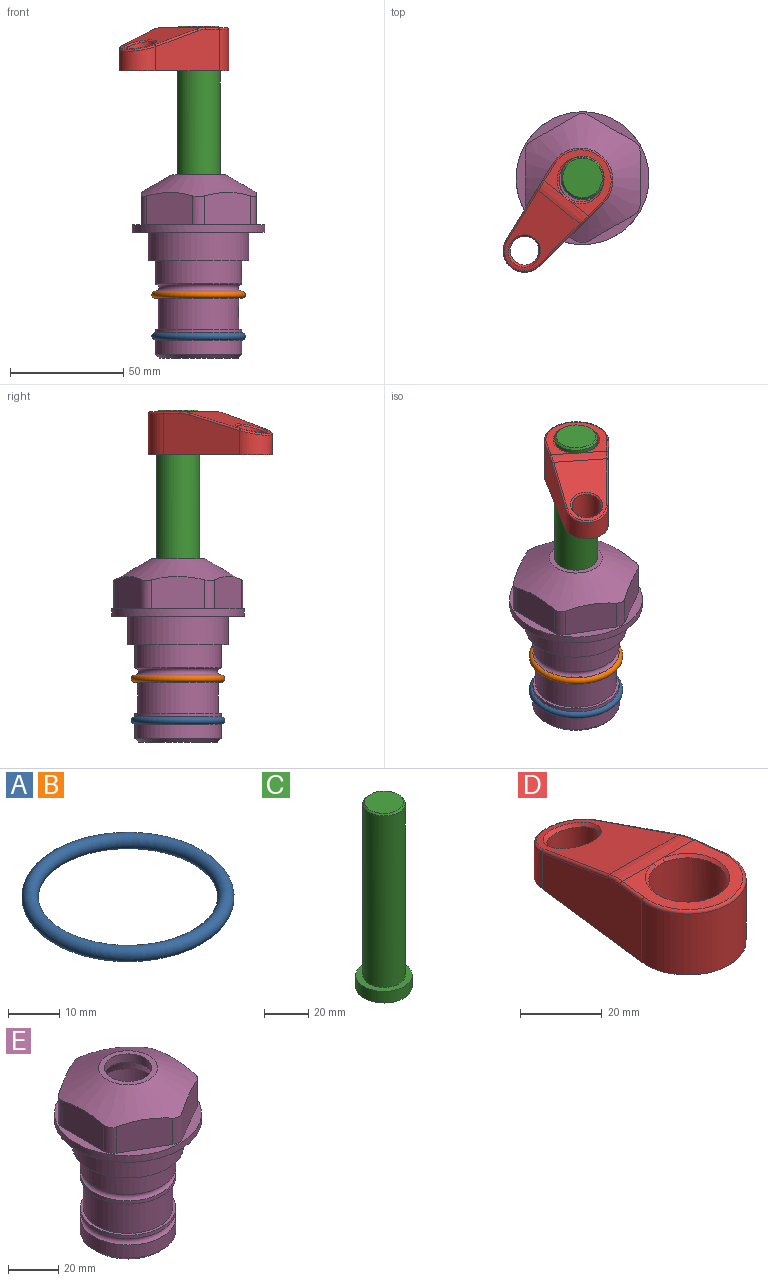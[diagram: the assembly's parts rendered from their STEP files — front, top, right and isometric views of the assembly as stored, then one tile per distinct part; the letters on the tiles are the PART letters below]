
ASSEMBLY  parts=5 mates=4
PART A: 1 faces, bbox 44.7x44.7x3.2 mm
  f0: torus R=19.05mm, axis (0,0,1), area 1193.9mm2
PART B: same geometry as A
PART C: 6 faces, bbox 25.4x25.4x101.6 mm
  f0: plane 17.46x17.46mm, normal (0,0,1), area 239.5mm2, adj f5
  f1: plane 25.4x25.4mm, normal (0,0,-1), area 506.7mm2, adj f2
  f2: cylinder r=12.7mm len=25.4mm, axis (0,0,1), area 506.7mm2, adj f1,f3
  f3: plane 25.4x25.4mm, normal (0,0,1), area 221.7mm2, adj f2,f4
  f4: cylinder r=9.53mm len=94.46mm, axis (0,0,1), area 5653mm2, adj f3,f5
  f5: cone r=8.73mm half-angle=45deg, axis (0,0,-1), area 64.4mm2, adj f0,f4
PART D: 31 faces, bbox 31.7x65.5x19.8 mm
  f0: plane 39.12x18.26mm, normal (0.99,0.12,0), area 612.2mm2, adj f1,f4,f7,f11,f13,f15
  f1: cylinder r=9.53mm len=18.91mm, axis (0,0,-1), area 296.1mm2, adj f0,f2,f7,f17
  f2: plane 39.12x18.26mm, normal (-0.99,0.12,0), area 612.2mm2, adj f1,f4,f7,f12,f14,f16
  f3: cylinder r=6.35mm len=12.7mm, axis (0,0,-1), area 362.4mm2, adj f7,f18
  f4: cylinder r=14.29mm len=28.58mm, axis (0,0,-1), area 882.2mm2, adj f0,f2,f7,f10
  f5: cylinder r=9.53mm len=19.05mm, axis (0,0,-1), area 1092.6mm2, adj f7,f19,f20
  f6: plane 26.99x23.69mm, normal (0,0,1), area 216.2mm2, adj f9,f10,f11,f12,f19
  f7: plane 63.5x28.58mm, normal (0,0,-1), area 661.8mm2, adj f0,f1,f2,f3,f4,f5,f22,f23
  f8: plane 33.52x23.6mm, normal (0,0.26,0.97), area 486mm2, adj f9,f15,f16,f17,f18
  f9: cylinder r=19.05mm len=24.72mm, axis (1,0,0), area 120.4mm2, adj f6,f8,f13,f14,f20
  f10: torus R=13.49mm, axis (0,0,1), area 59mm2, adj f4,f6,f11,f12
  f11: cylinder r=0.79mm len=8.67mm, axis (0.12,-0.99,0), area 10.8mm2, adj f0,f6,f10,f13
  f12: cylinder r=0.79mm len=8.67mm, axis (0.12,0.99,0), area 10.8mm2, adj f2,f6,f10,f14
  f13: bspline ~4.95x1.42mm, area 6.1mm2, adj f0,f9,f11,f15
  f14: bspline ~4.95x1.42mm, area 6.1mm2, adj f2,f9,f12,f16
  f15: cylinder r=0.79mm len=25.95mm, axis (0.12,-0.96,0.26), area 32.9mm2, adj f0,f8,f13,f17
  f16: cylinder r=0.79mm len=25.95mm, axis (0.12,0.96,-0.26), area 32.9mm2, adj f2,f8,f14,f17
  f17: bspline ~18.91x8.38mm, area 30mm2, adj f1,f8,f15,f16
  f18: bspline ~14.29x14.29mm, area 48.3mm2, adj f3,f8
  f19: cone r=9.53mm half-angle=45deg, axis (0,0,1), area 66.5mm2, adj f5,f6,f20
  f20: bspline ~3.22x0.96mm, area 3.5mm2, adj f5,f9,f19
  f21: plane 2.75x2.72mm, normal (0,0,-1), area 2.9mm2, adj f23,f25,f28
  f22: plane 23.05x15.88mm, normal (-0.99,-0.12,0), area 323.6mm2, adj f7,f25,f26,f27,f28,f29
  f23: plane 23.05x15.88mm, normal (0.99,-0.12,0), area 323.6mm2, adj f7,f21,f25,f27,f28,f30
  f24: cylinder r=9.53mm len=10.69mm, axis (0,0,-1), area 114.7mm2, adj f7,f27,f29,f30
  f25: cylinder r=12.7mm len=20.59mm, axis (0,0,-1), area 381.1mm2, adj f7,f21,f22,f23,f26,f28
  f26: plane 2.75x2.72mm, normal (0,0,-1), area 2.9mm2, adj f22,f25,f28
  f27: plane 19.72x18.37mm, normal (0,-0.26,-0.97), area 291.8mm2, adj f22,f23,f24,f28,f29,f30
  f28: cylinder r=15.88mm len=19.92mm, axis (1,0,0), area 54.8mm2, adj f21,f22,f23,f25,f26,f27
  f29: cylinder r=1.59mm len=11mm, axis (0,0,-1), area 34.7mm2, adj f7,f22,f24,f27
  f30: cylinder r=1.59mm len=11mm, axis (0,0,-1), area 34.7mm2, adj f7,f23,f24,f27
PART E: 36 faces, bbox 58.7x58.7x81 mm
  f0: cylinder r=17.78mm len=35.56mm, axis (0,0,1), area 1670.8mm2, adj f23,f24,f31
  f1: cylinder r=19.05mm len=38.1mm, axis (0,0,1), area 1191.9mm2, adj f26,f27,f30
  f2: plane 58.66x58.66mm, normal (0,0,-1), area 1150.6mm2, adj f3,f28
  f3: cylinder r=29.33mm len=58.66mm, axis (0,0,-1), area 585.1mm2, adj f2,f4
  f4: plane 58.66x58.66mm, normal (0,0,1), area 475.9mm2, adj f3,f5,f6,f7,f8,f9,f10,f11
  f5: plane 20.32x14.34mm, normal (-0.5,0.87,0), area 324.4mm2, adj f4,f15,f16,f17
  f6: plane 20.32x14.34mm, normal (0.5,0.87,0), area 324.4mm2, adj f4,f14,f15,f17
  f7: plane 23.48x14.34mm, normal (1,0,0), area 324.4mm2, adj f4,f13,f14,f17
  f8: plane 20.32x14.34mm, normal (0.5,-0.87,0), area 324.4mm2, adj f4,f12,f13,f17
  f9: plane 20.32x14.34mm, normal (-0.5,-0.87,0), area 324.4mm2, adj f4,f11,f12,f17
  f10: plane 23.48x14.34mm, normal (-1,0,0), area 324.4mm2, adj f4,f11,f16,f17
  f11: cylinder r=5.08mm len=12.85mm, axis (0,0,-1), area 67.2mm2, adj f4,f9,f10,f17
  f12: cylinder r=5.08mm len=12.85mm, axis (0,0,-1), area 67.2mm2, adj f4,f8,f9,f17
  f13: cylinder r=5.08mm len=12.85mm, axis (0,0,-1), area 67.2mm2, adj f4,f7,f8,f17
  f14: cylinder r=5.08mm len=12.85mm, axis (0,0,-1), area 67.2mm2, adj f4,f6,f7,f17
  f15: cylinder r=5.08mm len=12.85mm, axis (0,0,-1), area 67.2mm2, adj f4,f5,f6,f17
  f16: cylinder r=5.08mm len=12.85mm, axis (0,0,-1), area 67.2mm2, adj f4,f5,f10,f17
  f17: cone r=11.73mm half-angle=60deg, axis (0,0,-1), area 2071.8mm2, adj f5,f6,f7,f8,f9,f10,f11,f12
  f18: plane 23.46x23.46mm, normal (0,0,1), area 147.4mm2, adj f17,f35
  f19: plane 34.93x34.93mm, normal (0,0,-1), area 958mm2, adj f29
  f20: cylinder r=19.05mm len=38.1mm, axis (0,0,1), area 760.1mm2, adj f21,f29
  f21: torus R=19.05mm, axis (0,0,1), area 565.3mm2, adj f20,f22
  f22: cylinder r=19.05mm len=38.1mm, axis (0,0,1), area 190mm2, adj f21,f23
  f23: plane 38.1x38.1mm, normal (0,0,1), area 146.9mm2, adj f0,f22
  f24: plane 38.1x38.1mm, normal (0,0,-1), area 146.9mm2, adj f0,f25
  f25: cylinder r=19.05mm len=38.1mm, axis (0,0,1), area 190mm2, adj f24,f26
  f26: torus R=19.05mm, axis (0,0,1), area 565.3mm2, adj f1,f25
  f27: plane 44.45x44.45mm, normal (0,0,-1), area 411.7mm2, adj f1,f28
  f28: cylinder r=22.23mm len=44.45mm, axis (0,0,1), area 1773.5mm2, adj f2,f27
  f29: cone r=19.05mm half-angle=45deg, axis (0,0,1), area 257.5mm2, adj f19,f20
  f30: cylinder r=3.17mm len=6.75mm, axis (-1,0,0), area 128mm2, adj f1,f33
  f31: cylinder r=3.17mm len=6.35mm, axis (-1,0,0), area 102.5mm2, adj f0,f33
  f32: plane 25.4x25.4mm, normal (0,0,1), area 506.7mm2, adj f33
  f33: cylinder r=12.7mm len=66.42mm, axis (0,0,-1), area 5236.2mm2, adj f30,f31,f32,f34
  f34: cone r=9.53mm half-angle=30deg, axis (0,0,-1), area 443.4mm2, adj f33,f35
  f35: cylinder r=9.53mm len=19.05mm, axis (0,0,-1), area 240.9mm2, adj f18,f34
PLACE A t=(0,0,-21.59)mm
PLACE B t=(0,0,-3.18)mm
PLACE C rot(axis=(0,0,1),141.5deg) t=(0,0,27.55)mm
PLACE D rot(axis=(0,0,1),141.5deg) t=(-0.89,-1.12,26.76)mm
PLACE E at identity fixed
MATE fastened B.f0 <-> E.f0  axis (0,0,1) through (0,0,-27.69)mm
MATE fastened C.f2 <-> D.f6  axis (0,0,-1) through (0,0,90.26)mm
MATE cylindrical E.f0 <-> C.f2  axis (0,0,1) through (0,0,-50.55)mm
MATE fastened A.f0 <-> E.f0  axis (0,0,1) through (0,0,-46.1)mm
